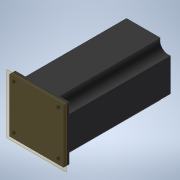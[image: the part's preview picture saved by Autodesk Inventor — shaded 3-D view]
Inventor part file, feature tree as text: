
AUTODESK INVENTOR PART (.ipt)
format: ipt  version: 2020 (Build 240168000, 168)  size: 125,952 bytes
history: native  units: mm
features: extrude x2, sketch x2
ambient origin geometry x8: Origin, YZ Plane, XZ Plane, XY Plane, X Axis, Y Axis, Z Axis, Center Point
bodies: Solid1 (feature_tree)
feature tree (4):
  extrude  "Extrusion1"  Depth=57.0mm
  extrude  "Extrusion2"  Depth=107.0mm
  sketch  "Sketch1"  dims[d0=57.0mm d1=57.0mm]
  sketch  "Sketch2"  dims[d2=5.0mm d3=5.0mm d4=5.0mm d5=113.0mm d6=0.0mm d7=107.0mm d8=0.0mm]
